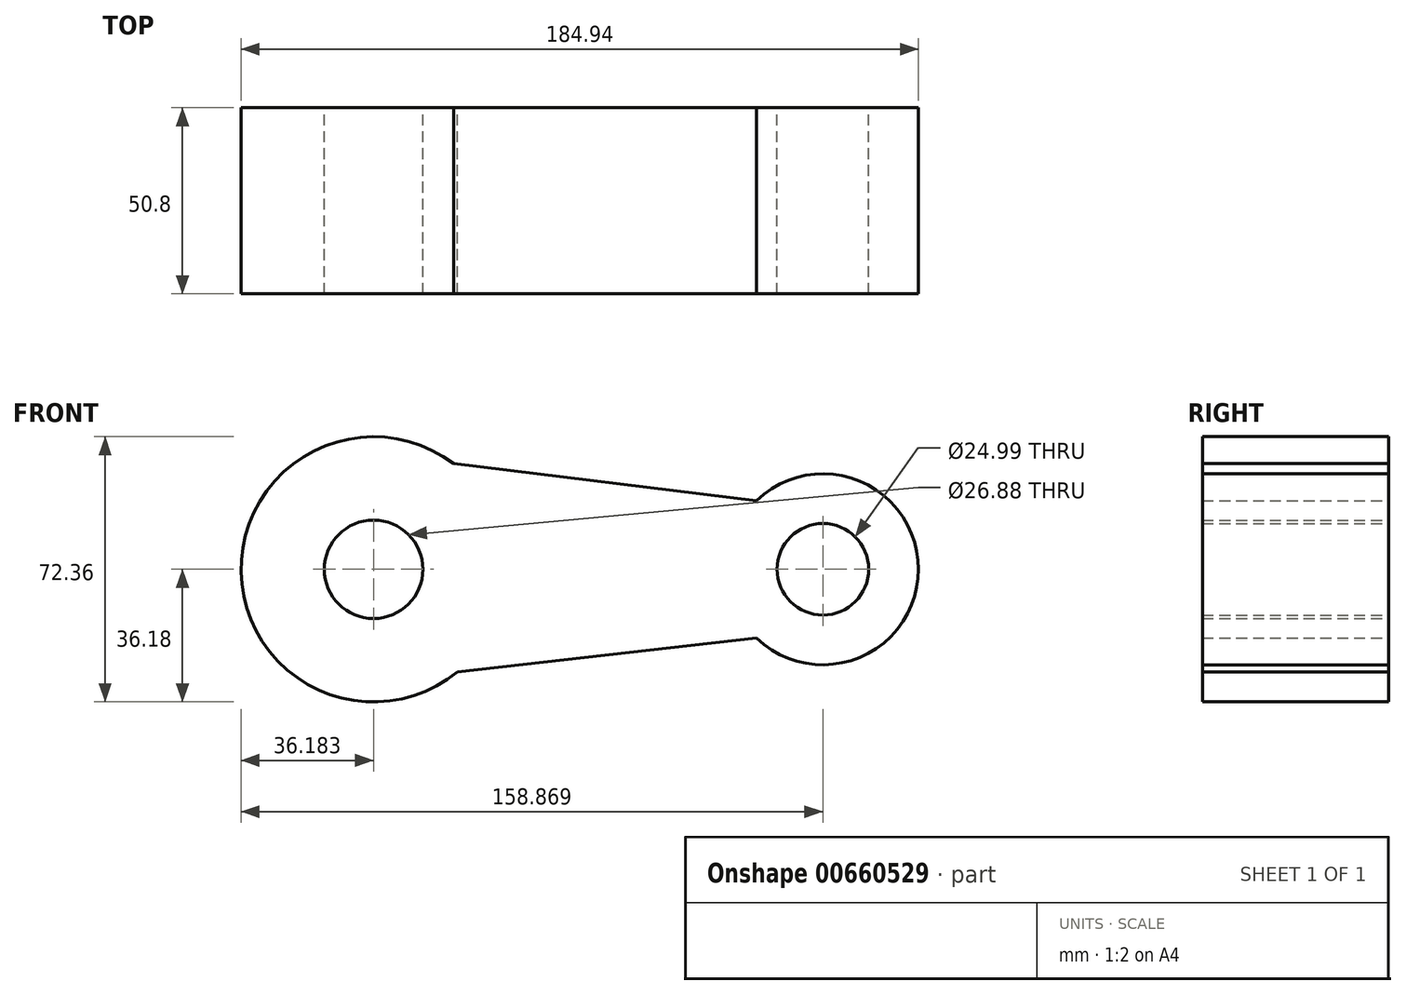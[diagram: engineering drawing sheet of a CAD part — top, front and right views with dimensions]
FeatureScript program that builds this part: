
annotation { "Feature Type Name" : "Feature", "Feature Type Description" : "" }
export const myFeature = defineFeature(function(context is Context, id is Id, definition is map)
    precondition{}
    {
        {
            var Q0;
            Q0=qCreatedBy(makeId("Front.planeOp"),FACE);
            var sketch = newSketch(context, id + "F0", { "sketchPlane" : qUnion([Q0])});
            skCircle(sketch, "E0", {"center": v(-67.55, 0) * mm, "radius": 36.18 * mm});
            skCircle(sketch, "E1", {"center": v(55.14, 0) * mm, "radius": 26.07 * mm});
            skCircle(sketch, "E2", {"center": v(55.14, 0) * mm, "radius": 12.5 * mm});
            skCircle(sketch, "E3", {"center": v(-67.55, 0) * mm, "radius": 13.44 * mm});
            skLineSegment(sketch, "E4", {"start": v(-45.7, 28.84) * mm, "end": v(37.05, 18.77) * mm});
            skLineSegment(sketch, "E5", {"start": v(-44.6, -27.98) * mm, "end": v(37.05, -18.77) * mm});
            skLineSegment(sketch, "E6", {"start": v(37.05, -18.77) * mm, "end": v(-44.6, -27.98) * mm});
            skSolve(sketch);
        }
        {
            var Q0;
            {var subQ0=sQuery(id+"F0.wireOp",EDGE,"E4");Q0=makeQuery(id+"F0.imprint","IMPRINT",FACE,{"disambiguationData":[TD([[makeQuery(id+"F0.imprint","IMPRINT",EDGE,{"derivedFrom":subQ0}),-1.0]])]});}
            var Q1;
            Q1 = qSketchRegion(id + "F0", true);
            var Q2;
            Q2=makeQuery(id+"F0.imprint","IMPRINT",FACE,{"disambiguationData":[TD([[makeQuery(id+"F0.imprint","IMPRINT",EDGE,{"derivedFrom":sQuery(id+"F0.wireOp",EDGE,"E2")}),-1.0]])]});
            var Q3;
            Q3=makeQuery(id+"F0.imprint","IMPRINT",FACE,{"disambiguationData":[TD([[makeQuery(id+"F0.imprint","IMPRINT",EDGE,{"derivedFrom":sQuery(id+"F0.wireOp",EDGE,"E3")}),-1.0]])]});
            extrude(context, id + "F1", {"entities" : qUnion([Q0, Q1, Q2, Q3]), "depth" : 50.8 * mm, "offsetDistance" : 25.4 * mm});
        }
    });
